# Revit family: HERZ-HERZCULES-Thermostatic Head M28x1.5 9860
name_source: partatom
category: Rohrzubehör
revit_build: Autodesk Revit 2018 (Build: 20190510_1515(x64)
units: mm (PartAtom-declared; Revit-internal decimal feet)

## family parameters
Arbeitsebenenbasiert = Nein
Beim Laden mit Abzugskörper schneiden = Nein
Bemaßung runder Anschluss = Durchmesser verwenden
Gemeinsam genutzt = Nein
Immer vertikal = Nein
OmniClass-Nummer = 23.65.55.14
OmniClass-Titel = Valves for Liquid Services
Teiletyp = Normal

## types (1)
- HERZ-HERZCULES-Thermostatic Head M28x1.5 9860
    Application = HERZCULES, thermostatic head for mounting on HERZ-Valves, suitable for thermostatic operation.
    Hand wheel = plastic, white
    Hersteller = HERZ Armaturen Ges.m.b.H.
    Model = HERZCULES, radiator thermostat in robust version
Protection against vandalism, theft and unauthorised operation.
Mounting, dismounting and set point control only possible with special tools.
Locked and concealed set point.
With automatic frost release.
    Operation = The HERZ-thermostat serves as a sensor and control element.
The change in volume of the liquid contained in the HERZ-hydrosensor actuates the valve spindle.
    Part number = 1986010
    S01 = 81 mm  [stored 0.265748 ft]
    S02 = 60 mm  [stored 0.19685 ft]
    Set value range = 8 - 26°C
    URL = www.herzvalves.com

note: [stored X ft] marks values corroborated as IEEE doubles in the binary element streams (Revit-internal decimal feet)
